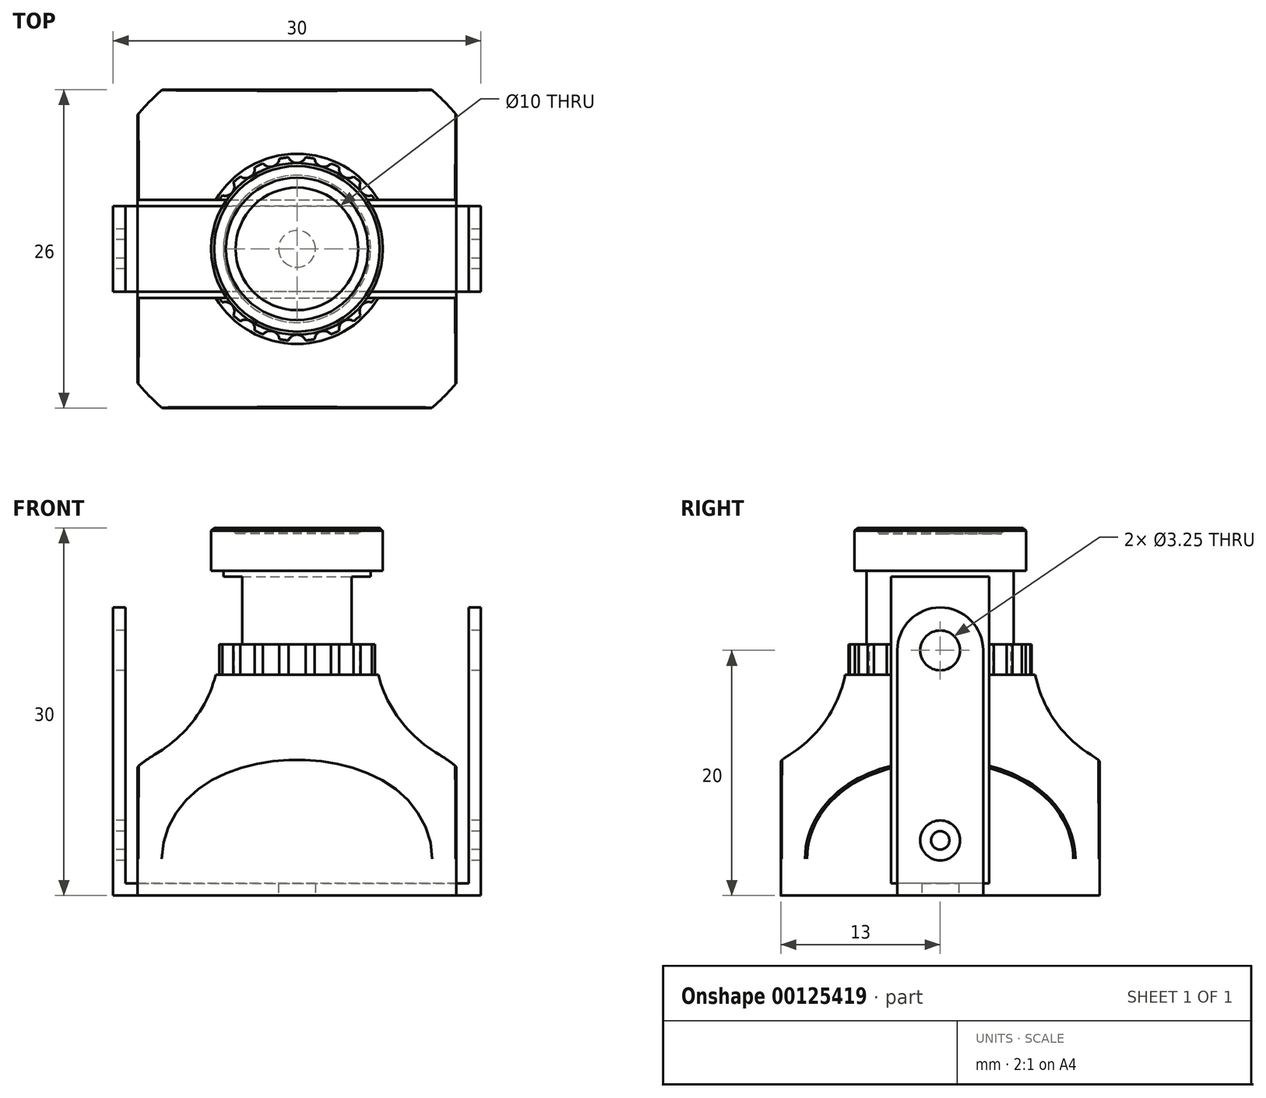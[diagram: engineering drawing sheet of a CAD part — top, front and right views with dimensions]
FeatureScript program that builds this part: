
annotation { "Feature Type Name" : "Feature", "Feature Type Description" : "" }
export const myFeature = defineFeature(function(context is Context, id is Id, definition is map)
    precondition{}
    {
        {
            var Q0;
            Q0=qCreatedBy(makeId("Front.planeOp"),FACE);
            var sketch = newSketch(context, id + "F0", { "sketchPlane" : qUnion([Q0])});
            skLineSegment(sketch, "E0", {"start": v(0, 83.46) * mm, "end": v(0, 0) * mm, "construction": true});
            skLineSegment(sketch, "E1", {"start": v(5, 30) * mm, "end": v(7, 30) * mm});
            skLineSegment(sketch, "E2", {"start": v(7, 30) * mm, "end": v(7, 26.5) * mm});
            skLineSegment(sketch, "E3", {"start": v(7, 26.5) * mm, "end": v(6, 26.5) * mm});
            skLineSegment(sketch, "E4", {"start": v(6, 26.5) * mm, "end": v(6, 20.5) * mm});
            skLineSegment(sketch, "E5", {"start": v(6, 20.5) * mm, "end": v(7.5, 20.5) * mm});
            skLineSegment(sketch, "E6", {"start": v(7.5, 20.5) * mm, "end": v(7.5, 18) * mm});
            skLineSegment(sketch, "E7", {"start": v(7.75, 18) * mm, "end": v(7.5, 18) * mm});
            skLineSegment(sketch, "E8", {"start": v(17, 3) * mm, "end": v(17, 0) * mm});
            skLineSegment(sketch, "E9", {"start": v(17, 0) * mm, "end": v(0, 0) * mm});
            skArc(sketch, "E10", {"start": v(7.75, 18) * mm, "mid": v(9.34, 14.28) * mm, "end": v(12.27, 11.5) * mm});
            skArc(sketch, "E11", {"start": v(17, 3) * mm, "mid": v(15.74, 7.86) * mm, "end": v(12.27, 11.5) * mm});
            skLineSegment(sketch, "E12", {"start": v(5, 30) * mm, "end": v(5, 29.5) * mm});
            skLineSegment(sketch, "E13", {"start": v(0, 29.36) * mm, "end": v(0, 0) * mm});
            skLineSegment(sketch, "E14", {"start": v(0, 29.86) * mm, "end": v(0, 29.36) * mm});
            skArc(sketch, "E15", {"start": v(5, 29.5) * mm, "mid": v(2.5, 29.77) * mm, "end": v(0, 29.86) * mm});
            skSolve(sketch);
        }
        {
            var Q0;
            Q0=makeQuery(id+"F0.imprint","IMPRINT",FACE,{"disambiguationData":[TD([[makeQuery(id+"F0.imprint","IMPRINT",EDGE,{"derivedFrom":sQuery(id+"F0.wireOp",EDGE,"E1")}),-1.0]])]});
            var Q1;
            Q1=sQuery(id+"F0.wireOp",EDGE,"E0");
            revolve(context, id + "F1", {"entities" : qUnion([Q0]), "axis" : qUnion([Q1]), "revolveType" : RevolveType.FULL});
        }
        {
            var Q0;
            Q0=makeQuery(id+"F1.opRevolve","SWEPT_FACE",FACE,{"disambiguationData":[OSD([sQuery(id+"F0.wireOp",EDGE,"E9")])]});
            var sketch = newSketch(context, id + "F2", { "sketchPlane" : qUnion([Q0])});
            skLineSegment(sketch, "E16.bottom", {"start": v(-13, 13) * mm, "end": v(13, 13) * mm});
            skLineSegment(sketch, "E16.top", {"start": v(-13, -13) * mm, "end": v(13, -13) * mm});
            skLineSegment(sketch, "E16.left", {"start": v(-13, 13) * mm, "end": v(-13, -13) * mm});
            skLineSegment(sketch, "E16.right", {"start": v(13, 13) * mm, "end": v(13, -13) * mm});
            skCircle(sketch, "E17", {"center": v(0, 0) * mm, "radius": 20 * mm});
            skSolve(sketch);
        }
        {
            var Q0;
            Q0 = qSketchRegion(id + "F2", true);
            extrude(context, id + "F3", {"entities" : qUnion([Q0]), "operationType" : NewBodyOperationType.REMOVE, "oppositeDirection" : true, "depth" : 15 * mm});
        }
        {
            var Q0;
            Q0=makeQuery(id+"F3.boolean.opBoolean","INTERSECT",EDGE,{"disambiguationData":[OD(1.0)],"derivedFrom":[makeQuery(id+"F1.opRevolve","SWEPT_FACE",FACE,{"disambiguationData":[OSD([sQuery(id+"F0.wireOp",EDGE,"E8")])]}),makeQuery(id+"F3.opExtrude","SWEPT_FACE",FACE,{"disambiguationData":[OSD([sQuery(id+"F2.wireOp",EDGE,"E16.left")])]})]});
            var Q1;
            Q1=makeQuery(id+"F3.boolean.opBoolean","INTERSECT",EDGE,{"disambiguationData":[OD(1.0)],"derivedFrom":[makeQuery(id+"F1.opRevolve","SWEPT_FACE",FACE,{"disambiguationData":[OSD([sQuery(id+"F0.wireOp",EDGE,"E11")])]}),makeQuery(id+"F3.opExtrude","SWEPT_FACE",FACE,{"disambiguationData":[OSD([sQuery(id+"F2.wireOp",EDGE,"E16.left")])]})]});
            var Q2;
            Q2=makeQuery(id+"F3.boolean.opBoolean","INTERSECT",EDGE,{"derivedFrom":[makeQuery(id+"F1.opRevolve","SWEPT_FACE",FACE,{"disambiguationData":[OSD([sQuery(id+"F0.wireOp",EDGE,"E10")])]}),makeQuery(id+"F3.opExtrude","SWEPT_FACE",FACE,{"disambiguationData":[OSD([sQuery(id+"F2.wireOp",EDGE,"E16.left")])]})]});
            var Q3;
            Q3=makeQuery(id+"F3.boolean.opBoolean","INTERSECT",EDGE,{"disambiguationData":[OD(0.0)],"derivedFrom":[makeQuery(id+"F1.opRevolve","SWEPT_FACE",FACE,{"disambiguationData":[OSD([sQuery(id+"F0.wireOp",EDGE,"E11")])]}),makeQuery(id+"F3.opExtrude","SWEPT_FACE",FACE,{"disambiguationData":[OSD([sQuery(id+"F2.wireOp",EDGE,"E16.left")])]})]});
            var Q4;
            Q4=makeQuery(id+"F3.boolean.opBoolean","INTERSECT",EDGE,{"disambiguationData":[OD(0.0)],"derivedFrom":[makeQuery(id+"F1.opRevolve","SWEPT_FACE",FACE,{"disambiguationData":[OSD([sQuery(id+"F0.wireOp",EDGE,"E8")])]}),makeQuery(id+"F3.opExtrude","SWEPT_FACE",FACE,{"disambiguationData":[OSD([sQuery(id+"F2.wireOp",EDGE,"E16.left")])]})]});
            var Q5;
            Q5=makeQuery(id+"F3.boolean.opBoolean","INTERSECT",EDGE,{"disambiguationData":[OD(0.0)],"derivedFrom":[makeQuery(id+"F1.opRevolve","SWEPT_FACE",FACE,{"disambiguationData":[OSD([sQuery(id+"F0.wireOp",EDGE,"E8")])]}),makeQuery(id+"F3.opExtrude","SWEPT_FACE",FACE,{"disambiguationData":[OSD([sQuery(id+"F2.wireOp",EDGE,"E16.top")])]})]});
            var Q6;
            Q6=makeQuery(id+"F3.boolean.opBoolean","INTERSECT",EDGE,{"disambiguationData":[OD(1.0)],"derivedFrom":[makeQuery(id+"F1.opRevolve","SWEPT_FACE",FACE,{"disambiguationData":[OSD([sQuery(id+"F0.wireOp",EDGE,"E8")])]}),makeQuery(id+"F3.opExtrude","SWEPT_FACE",FACE,{"disambiguationData":[OSD([sQuery(id+"F2.wireOp",EDGE,"E16.right")])]})]});
            var Q7;
            Q7=makeQuery(id+"F3.boolean.opBoolean","INTERSECT",EDGE,{"disambiguationData":[OD(1.0)],"derivedFrom":[makeQuery(id+"F1.opRevolve","SWEPT_FACE",FACE,{"disambiguationData":[OSD([sQuery(id+"F0.wireOp",EDGE,"E8")])]}),makeQuery(id+"F3.opExtrude","SWEPT_FACE",FACE,{"disambiguationData":[OSD([sQuery(id+"F2.wireOp",EDGE,"E16.bottom")])]})]});
            fillet(context, id + "F4", {"entities" : qUnion([Q0, Q1, Q2, Q3, Q4, Q5, Q6, Q7]), "radius" : 0.25 * mm, "tangentPropagation" : true, "allowEdgeOverflow" : false});
        }
        {
            var Q0;
            Q0=makeQuery(id+"F1.opRevolve","SWEPT_FACE",FACE,{"disambiguationData":[OSD([sQuery(id+"F0.wireOp",EDGE,"E5")])]});
            var sketch = newSketch(context, id + "F5", { "sketchPlane" : qUnion([Q0])});
            skCircle(sketch, "E18", {"center": v(0, 7.75) * mm, "radius": 0.75 * mm});
            skCircle(sketch, "E19.1.0", {"center": v(-2.18, 7.44) * mm, "radius": 0.75 * mm});
            skCircle(sketch, "E19.2.0", {"center": v(-4.19, 6.52) * mm, "radius": 0.75 * mm});
            skCircle(sketch, "E19.3.0", {"center": v(-5.86, 5.08) * mm, "radius": 0.75 * mm});
            skCircle(sketch, "E19.4.0", {"center": v(-7.05, 3.22) * mm, "radius": 0.75 * mm});
            skCircle(sketch, "E19.5.0", {"center": v(-7.67, 1.1) * mm, "radius": 0.75 * mm});
            skCircle(sketch, "E19.6.0", {"center": v(-7.67, -1.1) * mm, "radius": 0.75 * mm});
            skCircle(sketch, "E19.7.0", {"center": v(-7.05, -3.22) * mm, "radius": 0.75 * mm});
            skCircle(sketch, "E19.8.0", {"center": v(-5.86, -5.08) * mm, "radius": 0.75 * mm});
            skCircle(sketch, "E19.9.0", {"center": v(-4.19, -6.52) * mm, "radius": 0.75 * mm});
            skCircle(sketch, "E19.10.0", {"center": v(-2.18, -7.44) * mm, "radius": 0.75 * mm});
            skCircle(sketch, "E19.11.0", {"center": v(0, -7.75) * mm, "radius": 0.75 * mm});
            skCircle(sketch, "E19.12.0", {"center": v(2.18, -7.44) * mm, "radius": 0.75 * mm});
            skCircle(sketch, "E19.13.0", {"center": v(4.19, -6.52) * mm, "radius": 0.75 * mm});
            skCircle(sketch, "E19.14.0", {"center": v(5.86, -5.08) * mm, "radius": 0.75 * mm});
            skCircle(sketch, "E19.15.0", {"center": v(7.05, -3.22) * mm, "radius": 0.75 * mm});
            skCircle(sketch, "E19.16.0", {"center": v(7.67, -1.1) * mm, "radius": 0.75 * mm});
            skCircle(sketch, "E19.17.0", {"center": v(7.67, 1.1) * mm, "radius": 0.75 * mm});
            skCircle(sketch, "E19.18.0", {"center": v(7.05, 3.22) * mm, "radius": 0.75 * mm});
            skCircle(sketch, "E19.19.0", {"center": v(5.86, 5.08) * mm, "radius": 0.75 * mm});
            skCircle(sketch, "E19.20.0", {"center": v(4.19, 6.52) * mm, "radius": 0.75 * mm});
            skCircle(sketch, "E19.21.0", {"center": v(2.18, 7.44) * mm, "radius": 0.75 * mm});
            skPoint(sketch, "E19.center", {"position": v(0, 0) * mm});
            skCircle(sketch, "E20", {"center": v(0, 0) * mm, "radius": 7.75 * mm, "construction": true});
            skLineSegment(sketch, "E21", {"start": v(0, 7.75) * mm, "end": v(0, 0) * mm, "construction": true});
            skLineSegment(sketch, "E22", {"start": v(0, 0) * mm, "end": v(2.18, 7.44) * mm, "construction": true});
            skSolve(sketch);
        }
        {
            var Q0;
            Q0 = qSketchRegion(id + "F5", true);
            extrude(context, id + "F6", {"entities" : qUnion([Q0]), "operationType" : NewBodyOperationType.REMOVE, "oppositeDirection" : true, "depth" : 2.5 * mm});
        }
        {
            var Q0;
            Q0=makeQuery(id+"F1.opRevolve","SWEPT_EDGE",EDGE,{"disambiguationData":[OSD([sQuery(id+"F0.wireOp",EDGE,"E1"),sQuery(id+"F0.wireOp",EDGE,"E2")])]});
            chamfer(context, id + "F7", {"entities" : qUnion([Q0]), "width" : 0.25 * mm, "tangentPropagation" : true});
        }
        {
            var Q0;
            Q0=makeQuery(id+"F1.opRevolve","SWEPT_EDGE",EDGE,{"disambiguationData":[OSD([sQuery(id+"F0.wireOp",EDGE,"E1"),sQuery(id+"F0.wireOp",EDGE,"E12")])]});
            chamfer(context, id + "F8", {"entities" : qUnion([Q0]), "chamferType" : ChamferType.TWO_OFFSETS, "width1" : 0.4 * mm, "oppositeDirection" : false, "width2" : 0.8 * mm, "tangentPropagation" : true});
        }
        {
            var Q0;
            Q0=qCreatedBy(makeId("Right.planeOp"),FACE);
            var sketch = newSketch(context, id + "F9", { "sketchPlane" : qUnion([Q0])});
            skCircle(sketch, "E23", {"center": v(0, 4.5) * mm, "radius": 2.25 * mm});
            skSolve(sketch);
        }
        {
            var Q0;
            Q0 = qSketchRegion(id + "F9", true);
            extrude(context, id + "F10", {"entities" : qUnion([Q0]), "operationType" : NewBodyOperationType.ADD, "endBound" : BoundingType.SYMMETRIC, "depth" : 28 * mm});
        }
        {
            var Q0;
            Q0=qCreatedBy(makeId("Right.planeOp"),FACE);
            var sketch = newSketch(context, id + "F11", { "sketchPlane" : qUnion([Q0])});
            skCircle(sketch, "E24", {"center": v(0, 4.5) * mm, "radius": 1.63 * mm});
            skCircle(sketch, "E25", {"center": v(0, 4.5) * mm, "radius": 0.75 * mm});
            skSolve(sketch);
        }
        {
            var Q0;
            Q0 = qSketchRegion(id + "F11", true);
            extrude(context, id + "F12", {"entities" : qUnion([Q0]), "operationType" : NewBodyOperationType.ADD, "endBound" : BoundingType.SYMMETRIC, "depth" : 30 * mm});
        }
        {
            var Q0;
            Q0=qCreatedBy(makeId("Right.planeOp"),FACE);
            var sketch = newSketch(context, id + "F13", { "sketchPlane" : qUnion([Q0])});
            skArc(sketch, "E26", {"start": v(3.5, 20) * mm, "mid": v(0, 23.5) * mm, "end": v(-3.5, 20) * mm});
            skLineSegment(sketch, "E27", {"start": v(-3.5, 20) * mm, "end": v(-3.5, 0) * mm});
            skLineSegment(sketch, "E28", {"start": v(-3.5, 0) * mm, "end": v(3.5, 0) * mm});
            skLineSegment(sketch, "E29", {"start": v(3.5, 0) * mm, "end": v(3.5, 20) * mm});
            skCircle(sketch, "E30", {"center": v(0, 20) * mm, "radius": 1.63 * mm});
            skSolve(sketch);
        }
        {
            var Q0;
            Q0 = qSketchRegion(id + "F13", true);
            extrude(context, id + "F14", {"entities" : qUnion([Q0]), "endBound" : BoundingType.SYMMETRIC, "depth" : 30 * mm});
        }
        {
            var Q0;
            Q0=qCreatedBy(makeId("Front.planeOp"),FACE);
            var sketch = newSketch(context, id + "F15", { "sketchPlane" : qUnion([Q0])});
            skLineSegment(sketch, "E31.bottom", {"start": v(-14, 26) * mm, "end": v(14, 26) * mm});
            skLineSegment(sketch, "E31.top", {"start": v(-14, 1) * mm, "end": v(14, 1) * mm});
            skLineSegment(sketch, "E31.left", {"start": v(-14, 26) * mm, "end": v(-14, 1) * mm});
            skLineSegment(sketch, "E31.right", {"start": v(14, 26) * mm, "end": v(14, 1) * mm});
            skSolve(sketch);
        }
        {
            var Q0;
            Q0 = qSketchRegion(id + "F15", true);
            extrude(context, id + "F16", {"entities" : qUnion([Q0]), "operationType" : NewBodyOperationType.REMOVE, "endBound" : BoundingType.SYMMETRIC, "oppositeDirection" : true, "depth" : 8 * mm});
        }
        {
            var Q0;
            Q0=qCreatedBy(makeId("Top.planeOp"),FACE);
            var sketch = newSketch(context, id + "F17", { "sketchPlane" : qUnion([Q0])});
            skCircle(sketch, "E32", {"center": v(0, 0) * mm, "radius": 1.5 * mm});
            skSolve(sketch);
        }
        {
            var Q0;
            Q0 = qSketchRegion(id + "F17", true);
            extrude(context, id + "F18", {"entities" : qUnion([Q0]), "operationType" : NewBodyOperationType.REMOVE, "depth" : 2 * mm});
        }
    });
